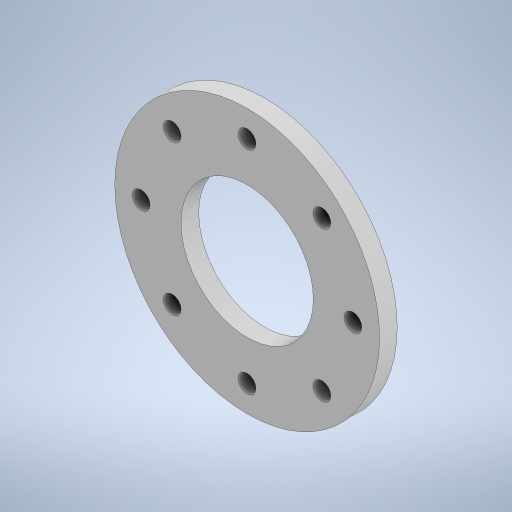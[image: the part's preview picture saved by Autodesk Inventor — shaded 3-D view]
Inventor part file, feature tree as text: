
AUTODESK INVENTOR PART (.ipt)
format: ipt  version: 2023 (Build 270158000, 158)  size: 253,952 bytes
history: native  units: mm
features: extrude x1, sketch x1
ambient origin geometry x8: Origin, YZ Plane, XZ Plane, XY Plane, X Axis, Y Axis, Z Axis, Center Point
bodies: Solido1 (feature_tree)
feature tree (2):
  extrude  "Estrusione1"  Depth=150.0mm
  sketch  "Schizzo1"
